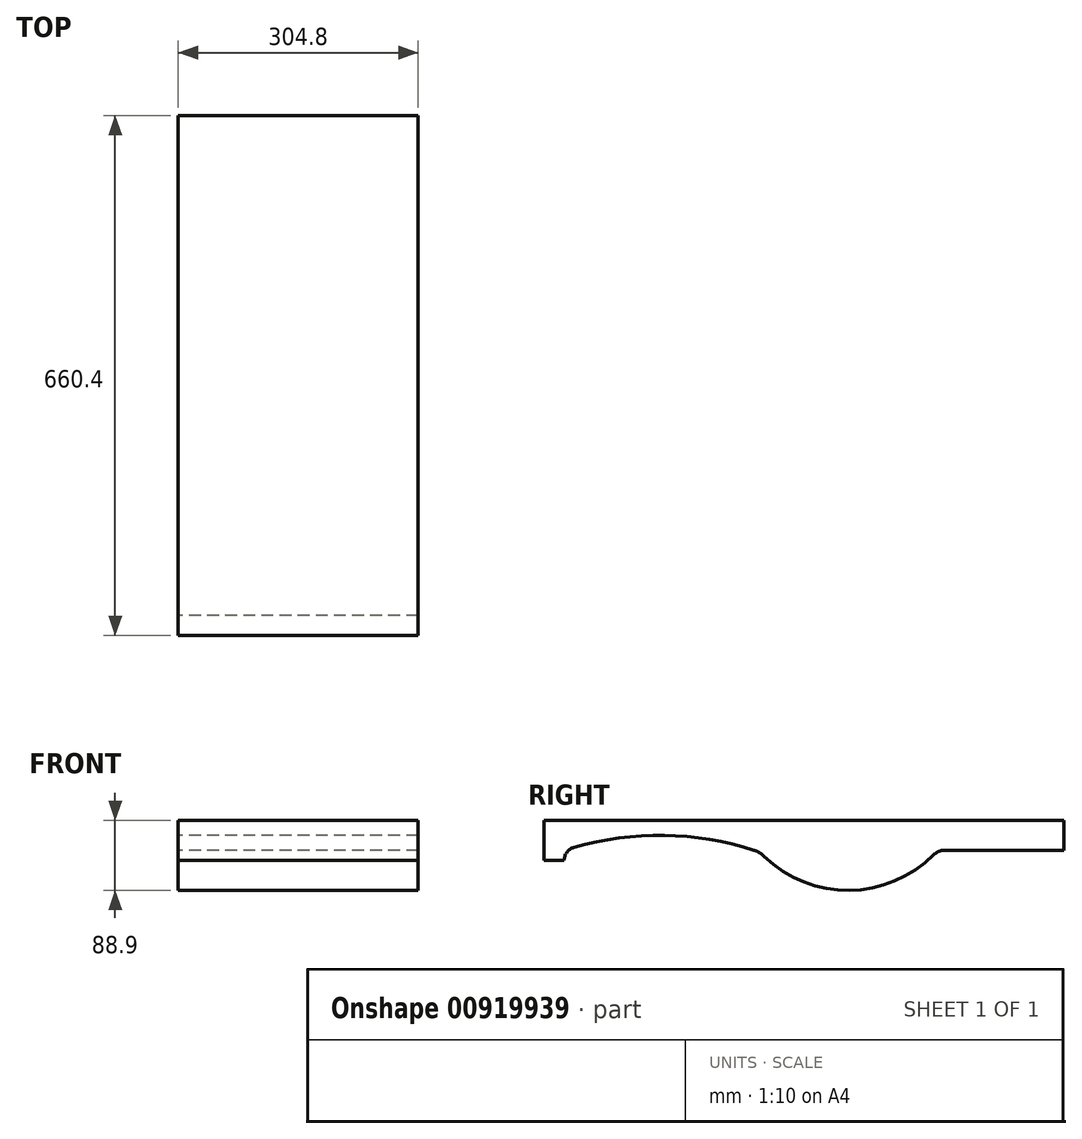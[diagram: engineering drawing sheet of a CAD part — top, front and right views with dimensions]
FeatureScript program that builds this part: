
annotation { "Feature Type Name" : "Feature", "Feature Type Description" : "" }
export const myFeature = defineFeature(function(context is Context, id is Id, definition is map)
    precondition{}
    {
        {
            var Q0;
            Q0=qCreatedBy(makeId("Right.planeOp"),FACE);
            var sketch = newSketch(context, id + "F0", { "sketchPlane" : qUnion([Q0])});
            skLineSegment(sketch, "E0", {"start": v(25.4, 0) * mm, "end": v(635, 0) * mm});
            skLineSegment(sketch, "E1", {"start": v(0, 19.05) * mm, "end": v(635, 19.05) * mm, "construction": true});
            skLineSegment(sketch, "E2", {"start": v(635, 0) * mm, "end": v(635, 69.85) * mm, "construction": true});
            skLineSegment(sketch, "E3", {"start": v(266.7, 0) * mm, "end": v(266.7, 69.85) * mm, "construction": true});
            skLineSegment(sketch, "E4", {"start": v(279.4, 0) * mm, "end": v(279.4, 62.22) * mm, "construction": true});
            skLineSegment(sketch, "E5", {"start": v(508, 0) * mm, "end": v(508, 69.85) * mm, "construction": true});
            skLineSegment(sketch, "E6", {"start": v(495.3, 64.55) * mm, "end": v(495.3, 0) * mm, "construction": true});
            skArc(sketch, "E7", {"start": v(279.4, 62.22) * mm, "mid": v(387.83, 19.06) * mm, "end": v(495.3, 64.55) * mm});
            skPoint(sketch, "E8", {"position": v(386.17, 19.05) * mm});
            skLineSegment(sketch, "E9", {"start": v(635, 69.85) * mm, "end": v(508, 69.85) * mm});
            skArc(sketch, "E10", {"start": v(495.3, 64.55) * mm, "mid": v(501.12, 68.47) * mm, "end": v(508, 69.85) * mm});
            skArc(sketch, "E11", {"start": v(266.7, 69.85) * mm, "mid": v(146.05, 88.9) * mm, "end": v(25.4, 69.85) * mm, "construction": true});
            skPoint(sketch, "E12", {"position": v(146.05, 88.9) * mm});
            skArc(sketch, "E13", {"start": v(279.4, 62.22) * mm, "mid": v(273.49, 66.76) * mm, "end": v(266.7, 69.85) * mm});
            skLineSegment(sketch, "E14", {"start": v(25.4, 0) * mm, "end": v(0, 0) * mm});
            skLineSegment(sketch, "E15", {"start": v(0, 0) * mm, "end": v(0, 56.87) * mm});
            skLineSegment(sketch, "E16", {"start": v(25.4, 69.85) * mm, "end": v(25.4, 0) * mm, "construction": true});
            skLineSegment(sketch, "E17", {"start": v(635, 69.85) * mm, "end": v(660.4, 69.85) * mm});
            skLineSegment(sketch, "E18", {"start": v(660.4, 69.85) * mm, "end": v(660.4, 0) * mm});
            skLineSegment(sketch, "E19", {"start": v(660.4, 0) * mm, "end": v(635, 0) * mm});
            skArc(sketch, "E20", {"start": v(38.1, 73.73) * mm, "mid": v(28.93, 67.42) * mm, "end": v(25.4, 56.87) * mm});
            skLineSegment(sketch, "E21", {"start": v(25.4, 56.87) * mm, "end": v(0, 56.87) * mm});
            skArc(sketch, "E22", {"start": v(266.7, 69.85) * mm, "mid": v(152.69, 88.84) * mm, "end": v(38.1, 73.73) * mm});
            skLineSegment(sketch, "E23", {"start": v(38.1, 73.73) * mm, "end": v(38.1, 0) * mm, "construction": true});
            skSolve(sketch);
        }
        {
            var Q0;
            Q0=qCreatedBy(makeId("Right.planeOp"),FACE);
            var sketch = newSketch(context, id + "F1", { "sketchPlane" : qUnion([Q0])});
            skLineSegment(sketch, "E24.bottom", {"start": v(0, 0) * mm, "end": v(660.4, 0) * mm});
            skLineSegment(sketch, "E24.top", {"start": v(0, 107.95) * mm, "end": v(660.4, 107.95) * mm});
            skLineSegment(sketch, "E24.left", {"start": v(0, 0) * mm, "end": v(0, 107.95) * mm});
            skLineSegment(sketch, "E24.right", {"start": v(660.4, 0) * mm, "end": v(660.4, 107.95) * mm});
            skLineSegment(sketch, "E25", {"start": v(0, 88.9) * mm, "end": v(660.4, 88.9) * mm, "construction": true});
            skSolve(sketch);
        }
        {
            var Q0;
            Q0 = qSketchRegion(id + "F1", true);
            extrude(context, id + "F2", {"entities" : qUnion([Q0]), "depth" : 304.8 * mm, "offsetDistance" : 25.4 * mm});
        }
        {
            var Q0;
            Q0 = qSketchRegion(id + "F0", true);
            extrude(context, id + "F3", {"entities" : qUnion([Q0]), "operationType" : NewBodyOperationType.REMOVE, "endBound" : BoundingType.THROUGH_ALL, "depth" : 25.4 * mm, "offsetDistance" : 25.4 * mm});
        }
    });
